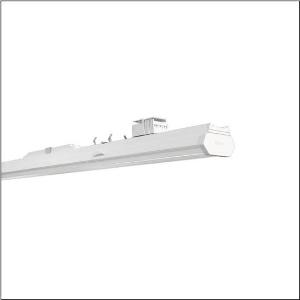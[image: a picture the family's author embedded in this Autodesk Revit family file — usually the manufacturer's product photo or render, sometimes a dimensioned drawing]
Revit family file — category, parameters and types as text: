
# Revit family: licross_r__11_protected_ho_51tp13mn4gxs_4b4b
name_source: partatom
category: Lighting Fixtures
units: mm (PartAtom-declared; Revit-internal decimal feet)

## family parameters
Cut with Voids When Loaded = No
Host = Face
Light Source = No
Part Type = Normal
Room Calculation Point = No
Round Connector Dimension = Use Diameter
Shared = No

## types (1)
- --- (1 x LED, 16110 lm, 87.4 W, 4000K)
    Apparent Load = 87 VA
    CIE Flux Codes = 89 96 99 100 99
    Color Rendering = 80
    Color Temperature = 4000K
    Default Elevation = 1800 mm
    Description = Licross® 11 Protected HO, luminaire insert, of sheet steel, galvanised, coil coated, white, length: 1.500mm, width: 90mm, height: 101mm, LED rated luminous flux: 16.110lm, light colour: 840, control gear: ON/OFF Multilumen, with plug, 3-pole, with phase selection, mains connection: 220..240V, AC, 50/60Hz, rated input power: 87W, halogen-free wiring, primary light control with lens, of plastic, primary optical cover: cover, of PMMA, light emission: direct distribution, primary light characteristic: symmetric, protection rating (complete): IP64, insulation class (complete): insulation class I (protective earthing), certification: CE, ENEC, VDE, UKCA, protection symbol: D if used in an environment with conductive dust loads with corresponding accessories, impact resistance: IK06, permissible ambient temperature for indoor applications: -35..+35°C, corresponds to IFS (International Featured Standards) requirements for safety and quality in the food industry, reducing of maximum allowable ambient temperature of 5°C with ceiling mounting, LABS conformity tested according to VDMA 24364:2018-05, packaging unit: 1 piece
    Height = 92 mm
    Lamp = 1 x LED
    Lamp Light Flux = 16110 lm
    Lamp Power = 87.4 W
    Lamp count = 1
    Length = 1500 mm
    Luminous efficacy = 184 lm/W
    Manufacturer = Siteco
    ModVariant = No
    Model = 51TP13MN4GXS
    Mounting Place = Ceiling
    Mounting Type = Pendant
    Number of Poles = 1
    OnlyDefault = Yes
    Power Factor = 1
    Product Name = Licross® 11 Protected HO
    Product group = luminaire insert
    ProductGroupID = 901
    Protection Class = Protection class I
    Protection Degree = IP 64
    RLX_Detail_Level = 1
    RLX_Emergency_Light_Flux = 0 lm
    RLX_Emergency_Type = 0
    RLX_Emergency_Type_DB = No
    RlxData = <blob elided: 22029 chars, md5=92246993>
    Socket = socket
    Standby Power = 0 W
    System Light Flux = 16110 lm
    System Power = 87 W
    Type Comments = factory setting: luminous flux: 100 % | (A | C | E) | 203 mA
    Type Image = l_1256148.jpg
    URL = http://relux.com
    VarID = @adj_055071
    Voltage = 0 V
    Weight = 0.00 kg
    Width = 88 mm

## geometry (parser evidence)
native form markers: Blend x4, Sweep x9
no freeform markers — native parametric forms only
